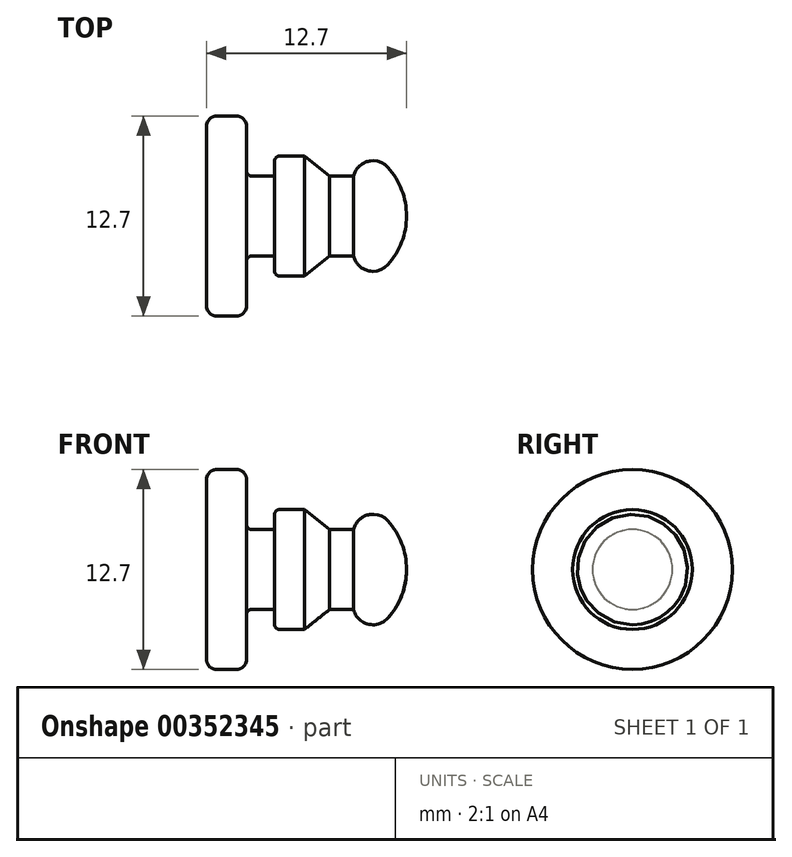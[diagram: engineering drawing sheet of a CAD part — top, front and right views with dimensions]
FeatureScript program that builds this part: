
annotation { "Feature Type Name" : "Feature", "Feature Type Description" : "" }
export const myFeature = defineFeature(function(context is Context, id is Id, definition is map)
    precondition{}
    {
        {
            var Q0;
            Q0=qCreatedBy(makeId("Front.planeOp"),FACE);
            var sketch = newSketch(context, id + "F0", { "sketchPlane" : qUnion([Q0])});
            skLineSegment(sketch, "E0", {"start": v(0, 0) * mm, "end": v(-12.7, 0) * mm});
            skLineSegment(sketch, "E1", {"start": v(-12.7, 0) * mm, "end": v(-12.7, 6.35) * mm});
            skLineSegment(sketch, "E2", {"start": v(-12.7, 6.35) * mm, "end": v(-10.16, 6.35) * mm});
            skLineSegment(sketch, "E3", {"start": v(-10.16, 6.35) * mm, "end": v(-10.16, 2.54) * mm});
            skLineSegment(sketch, "E4", {"start": v(-10.16, 2.54) * mm, "end": v(-8.38, 2.54) * mm});
            skLineSegment(sketch, "E5", {"start": v(-8.38, 2.54) * mm, "end": v(-8.38, 3.8) * mm});
            skLineSegment(sketch, "E6", {"start": v(-8.38, 3.8) * mm, "end": v(-6.48, 3.8) * mm});
            skLineSegment(sketch, "E7", {"start": v(-6.48, 3.8) * mm, "end": v(-4.89, 2.54) * mm});
            skLineSegment(sketch, "E8", {"start": v(-4.89, 2.54) * mm, "end": v(-3.36, 2.54) * mm});
            skLineSegment(sketch, "E9", {"start": v(-3.36, 2.54) * mm, "end": v(-3.36, 4.45) * mm});
            skArc(sketch, "E10", {"start": v(0, 0) * mm, "mid": v(-0.94, 2.79) * mm, "end": v(-3.36, 4.45) * mm});
            skSolve(sketch);
        }
        {
            var Q0;
            Q0=makeQuery(id+"F0.imprint","IMPRINT",FACE,{"disambiguationData":[TD([[makeQuery(id+"F0.imprint","IMPRINT",EDGE,{"derivedFrom":sQuery(id+"F0.wireOp",EDGE,"E0")}),-1.0]])]});
            var Q1;
            Q1=sQuery(id+"F0.wireOp",EDGE,"E0");
            revolve(context, id + "F1", {"entities" : qUnion([Q0]), "axis" : qUnion([Q1]), "revolveType" : RevolveType.FULL});
        }
        {
            var Q0;
            Q0=makeQuery(id+"F1.opRevolve","SWEPT_EDGE",EDGE,{"disambiguationData":[OSD([sQuery(id+"F0.wireOp",EDGE,"E1"),sQuery(id+"F0.wireOp",EDGE,"E2")])]});
            fillet(context, id + "F2", {"entities" : qUnion([Q0]), "radius" : 0.64 * mm, "tangentPropagation" : true, "allowEdgeOverflow" : false});
        }
        {
            var Q0;
            Q0=makeQuery(id+"F1.opRevolve","SWEPT_EDGE",EDGE,{"disambiguationData":[OSD([sQuery(id+"F0.wireOp",EDGE,"E2"),sQuery(id+"F0.wireOp",EDGE,"E3")])]});
            fillet(context, id + "F3", {"entities" : qUnion([Q0]), "radius" : 0.64 * mm, "tangentPropagation" : true, "allowEdgeOverflow" : false});
        }
        {
            var Q0;
            Q0=makeQuery(id+"F1.opRevolve","SWEPT_EDGE",EDGE,{"disambiguationData":[OSD([sQuery(id+"F0.wireOp",EDGE,"E5"),sQuery(id+"F0.wireOp",EDGE,"E6")])]});
            fillet(context, id + "F4", {"entities" : qUnion([Q0]), "radius" : 0.32 * mm, "tangentPropagation" : true, "allowEdgeOverflow" : false});
        }
        {
            var Q0;
            Q0=makeQuery(id+"F1.opRevolve","SWEPT_EDGE",EDGE,{"disambiguationData":[OSD([sQuery(id+"F0.wireOp",EDGE,"E3"),sQuery(id+"F0.wireOp",EDGE,"E4")])]});
            fillet(context, id + "F5", {"entities" : qUnion([Q0]), "radius" : 0.32 * mm, "tangentPropagation" : true, "allowEdgeOverflow" : false});
        }
        {
            var Q0;
            Q0=makeQuery(id+"F1.opRevolve","SWEPT_FACE",FACE,{"disambiguationData":[OSD([sQuery(id+"F0.wireOp",EDGE,"E10")])]});
            fillet(context, id + "F6", {"entities" : qUnion([Q0]), "radius" : 1.27 * mm, "tangentPropagation" : true, "allowEdgeOverflow" : false});
        }
    });
